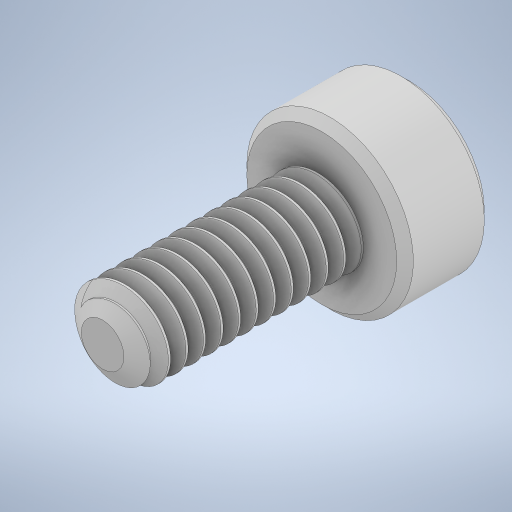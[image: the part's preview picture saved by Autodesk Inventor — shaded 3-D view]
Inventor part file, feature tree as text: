
AUTODESK INVENTOR PART (.ipt)
format: ipt  version: 2024 (Build 280153000, 153)  size: 676,864 bytes
history: native  units: mm
features: other x1, chamfer x1
ambient origin geometry x8: Origin, YZ Plane, XZ Plane, XY Plane, X Axis, Y Axis, Z Axis, Center Point
bodies: Body1 (feature_tree)
feature tree (2):
  other  "Těleso1"
  chamfer  "Chamfer1"  [1 undecoded]
note: 1 required parameter value undecoded (feature->parameter linkage not recoverable at this tier; creation-order binding heuristic only, values carry confidence <= 0.55)
